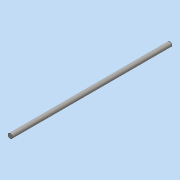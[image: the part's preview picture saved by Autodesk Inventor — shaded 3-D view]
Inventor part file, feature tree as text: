
AUTODESK INVENTOR PART (.ipt)
format: ipt  version: 2016 (Build 200138000, 138)  size: 86,016 bytes
history: native  units: mm
features: extrude x1, thread x1, sketch x1
ambient origin geometry x8: Origin, YZ Plane, XZ Plane, XY Plane, X Axis, Y Axis, Z Axis, Center Point
bodies: Solid1 (feature_tree)
feature tree (3):
  extrude  "Extrusion1"  Depth=275.0mm TaperAngle=0.0deg
  thread  "Thread1"  [1 undecoded]
  sketch  "Sketch1"  dims[d0=8.0mm d1=275.0mm d2=0.0mm d3=10.0mm d4=0.0mm]
note: 1 required parameter value undecoded (feature->parameter linkage not recoverable at this tier; creation-order binding heuristic only, values carry confidence <= 0.55)
